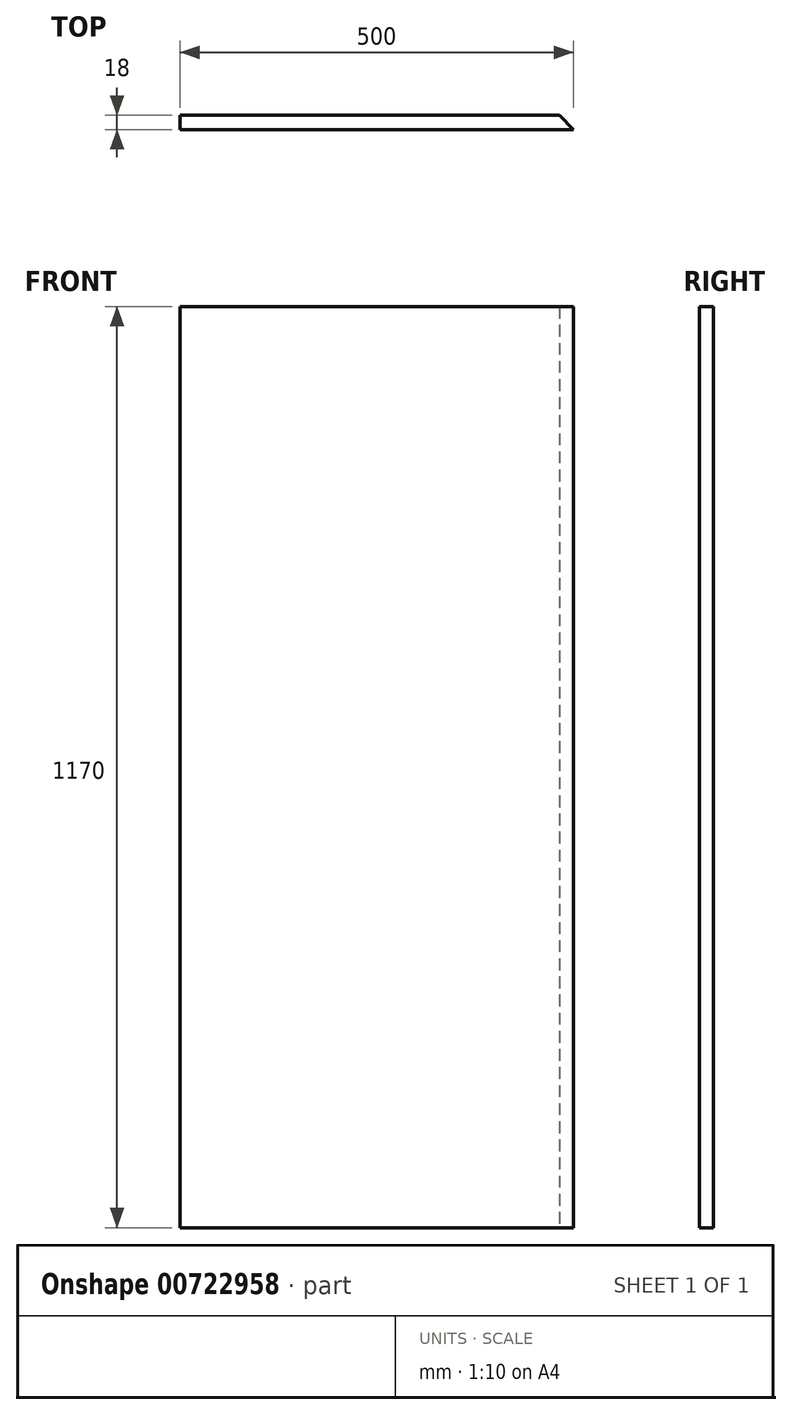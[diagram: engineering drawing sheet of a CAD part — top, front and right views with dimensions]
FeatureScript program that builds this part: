
annotation { "Feature Type Name" : "Feature", "Feature Type Description" : "" }
export const myFeature = defineFeature(function(context is Context, id is Id, definition is map)
    precondition{}
    {
        {
            var Q0;
            Q0=qCreatedBy(makeId("Front.planeOp"),FACE);
            var sketch = newSketch(context, id + "F0", { "sketchPlane" : qUnion([Q0])});
            skLineSegment(sketch, "E0.bottom", {"start": v(-250, 585) * mm, "end": v(250, 585) * mm});
            skLineSegment(sketch, "E0.top", {"start": v(-250, -585) * mm, "end": v(250, -585) * mm});
            skLineSegment(sketch, "E0.left", {"start": v(-250, 585) * mm, "end": v(-250, -585) * mm});
            skLineSegment(sketch, "E0.right", {"start": v(250, 585) * mm, "end": v(250, -585) * mm});
            skLineSegment(sketch, "E1", {"start": v(-250, 585) * mm, "end": v(250, -585) * mm});
            skLineSegment(sketch, "E2", {"start": v(250, 585) * mm, "end": v(-250, -585) * mm});
            skSolve(sketch);
        }
        {
            var Q0;
            Q0 = qSketchRegion(id + "F0", true);
            extrude(context, id + "F1", {"entities" : qUnion([Q0]), "depth" : 18 * mm, "offsetDistance" : 25 * mm});
        }
        {
            var Q0;
            Q0=makeQuery(id+"F1.opExtrude","CAP_EDGE",EDGE,{"disambiguationData":[OSD([sQuery(id+"F0.wireOp",EDGE,"E0.right")])],"isStart":true});
            chamfer(context, id + "F2", {"entities" : qUnion([Q0]), "width" : 18 * mm, "tangentPropagation" : true});
        }
    });
